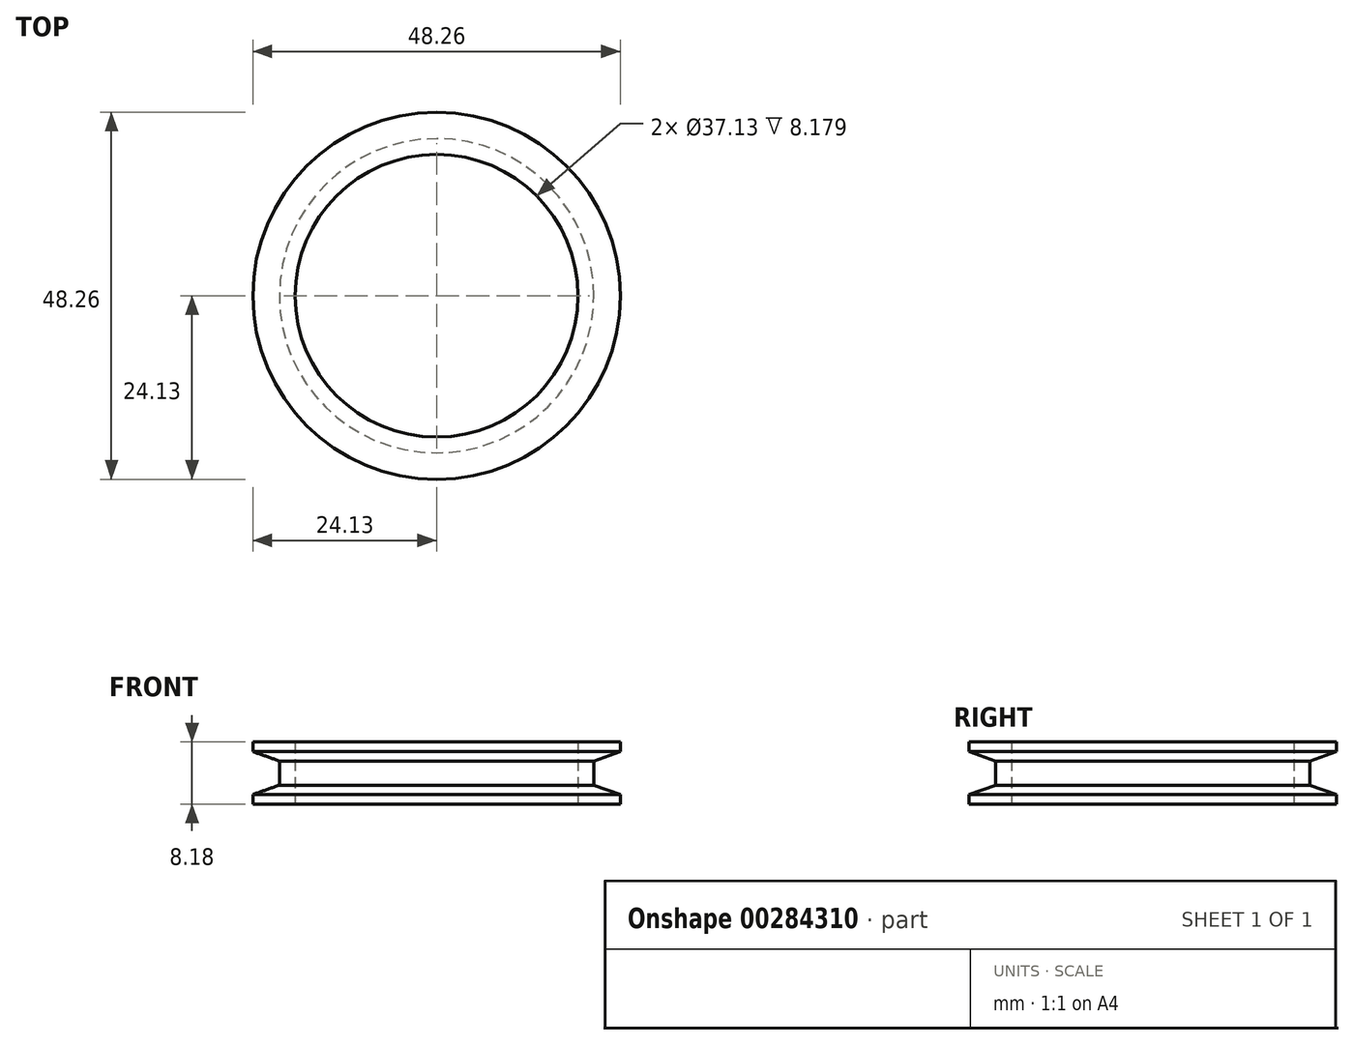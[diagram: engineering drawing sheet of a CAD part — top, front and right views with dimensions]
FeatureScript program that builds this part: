
annotation { "Feature Type Name" : "Feature", "Feature Type Description" : "" }
export const myFeature = defineFeature(function(context is Context, id is Id, definition is map)
    precondition{}
    {
        {
            var Q0;
            Q0=qCreatedBy(makeId("Front.planeOp"),FACE);
            var sketch = newSketch(context, id + "F0", { "sketchPlane" : qUnion([Q0])});
            skLineSegment(sketch, "E0", {"start": v(0, 0) * mm, "end": v(0, 10.43) * mm, "construction": true});
            skLineSegment(sketch, "E1", {"start": v(18.57, 0) * mm, "end": v(18.57, 8.18) * mm});
            skLineSegment(sketch, "E2", {"start": v(18.57, 8.18) * mm, "end": v(24.13, 8.18) * mm});
            skLineSegment(sketch, "E3", {"start": v(24.13, 8.18) * mm, "end": v(24.13, 6.9) * mm});
            skLineSegment(sketch, "E4", {"start": v(24.13, 6.9) * mm, "end": v(20.65, 5.68) * mm});
            skLineSegment(sketch, "E5", {"start": v(20.65, 5.68) * mm, "end": v(20.65, 2.5) * mm});
            skLineSegment(sketch, "E6", {"start": v(20.65, 2.5) * mm, "end": v(24.13, 1.27) * mm});
            skLineSegment(sketch, "E7", {"start": v(24.13, 1.27) * mm, "end": v(24.13, 0) * mm});
            skLineSegment(sketch, "E8", {"start": v(24.13, 0) * mm, "end": v(18.57, 0) * mm});
            skSolve(sketch);
        }
        {
            var Q0;
            Q0 = qSketchRegion(id + "F0", true);
            var Q1;
            Q1=sQuery(id+"F0.wireOp",EDGE,"E0");
            revolve(context, id + "F1", {"entities" : qUnion([Q0]), "axis" : qUnion([Q1]), "revolveType" : RevolveType.FULL});
        }
    });
